# Revit family: MP 800 Turbo (a)
name_source: partatom
category: Equipement spécialisé
revit_build: Autodesk Revit LT 2015 (Build: 20140606_1530(x64)
units: mm (PartAtom-declared; Revit-internal decimal feet)

## types (4) — shared parameters
Apparent Power = 0 VA
Depth = 188 mm  [stored 0.616798 ft]
Depth Electrique connexion = 94 mm  [stored 0.308399 ft]
Description = MIXERS PLONGEANTS GAMME LARGE
Fabricant = ROBOT COUPE
Height = 1160 mm
Height Electrique connexion = 1150 mm
Phase = 1
URL = www.robot-coupe.com
Width = 189 mm  [stored 0.620079 ft]
water = Connector
zero-valued in all types: Cold water supply, Cold water supply height, Used water, Waste water height

## per-type parameters (varying)
| type | Amps | Cycle | HP | Modèle | Speeds (Rpm) | Volts | Watts | Weight |
| MP 800 Turbo   230/50/1 | 4.5 A | 50 Hz |  | MP 800 Turbo | 9500 | 230 V | 1000 W | 9.2 kg |
| MP 800 Turbo   120/60/1 | 7.5 A | 60 Hz |  | MP 800 Turbo | 9500 | 120 V | 1000 W | 9.2 kg |
| MP 800 Turbo   240/50/1 | 2.1 A | 50 Hz |  | MP 800 Turbo | 9500 | 240 V | 1000 W | 9.2 kg |
| MP 800 Turbo USA   120/60/1 | 8.4 A | 60 Hz | 1.6 | MP 800 Turbo USA | 12000 | 120 V | 0 W | 21 lbs |

note: [stored X ft] marks values corroborated as IEEE doubles in the binary element streams (Revit-internal decimal feet)

## geometry (parser evidence)
native form markers: Blend x104, Sweep x10
no freeform markers — native parametric forms only
